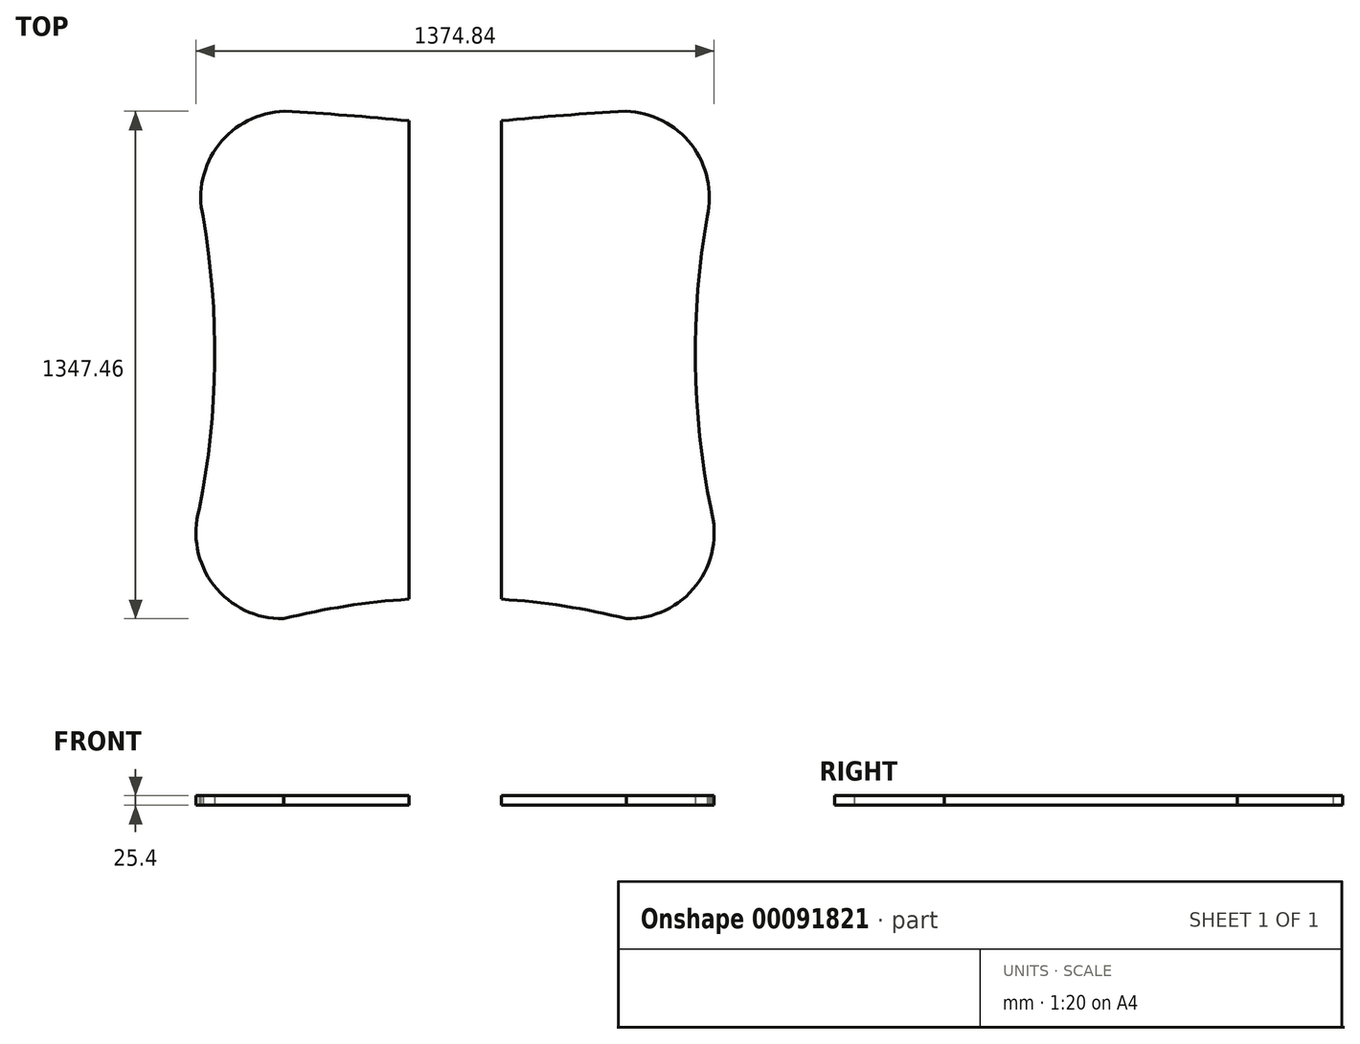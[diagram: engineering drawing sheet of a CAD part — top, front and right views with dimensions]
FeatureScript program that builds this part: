
annotation { "Feature Type Name" : "Feature", "Feature Type Description" : "" }
export const myFeature = defineFeature(function(context is Context, id is Id, definition is map)
    precondition{}
    {
        {
            var Q0;
            Q0=qCreatedBy(makeId("Top.planeOp"),FACE);
            var sketch = newSketch(context, id + "F0", { "sketchPlane" : qUnion([Q0])});
            skLineSegment(sketch, "E0", {"start": v(-122.75, 617.41) * mm, "end": v(-122.75, 363.41) * mm});
            skArc(sketch, "E1", {"start": v(-678.8, -413.88) * mm, "mid": v(-637.61, -25.7) * mm, "end": v(-668.85, 363.41) * mm});
            skArc(sketch, "E2", {"start": v(-452.95, 642.81) * mm, "mid": v(-626.87, 554.1) * mm, "end": v(-668.85, 363.41) * mm});
            skArc(sketch, "E3", {"start": v(-678.8, -413.88) * mm, "mid": v(-639.9, -615.57) * mm, "end": v(-454.8, -704.61) * mm});
            skLineSegment(sketch, "E4", {"start": v(-122.75, 617.41) * mm, "end": v(-122.75, -652.59) * mm});
            skArc(sketch, "E5", {"start": v(-122.75, 617.41) * mm, "mid": v(-287.7, 632.1) * mm, "end": v(-452.95, 642.81) * mm});
            skArc(sketch, "E6", {"start": v(-122.75, -652.59) * mm, "mid": v(-289.94, -671.12) * mm, "end": v(-454.8, -704.61) * mm});
            skSolve(sketch);
        }
        {
            var Q0;
            Q0=makeQuery(id+"F0.imprint","IMPRINT",FACE,{"disambiguationData":[TD([[makeQuery(id+"F0.imprint","IMPRINT",EDGE,{"derivedFrom":sQuery(id+"F0.wireOp",EDGE,"e7358e8d-3bd0-44fc-b618-9dafbb7d24566.MirrorCS")}),1.0]])]});
            var Q1;
            {var subQ0=sQuery(id+"F0.wireOp",EDGE,"E4");var subQ3=makeQuery(id+"F0.imprint","IMPRINT",VERTEX,{"derivedFrom":subQ0});Q1=makeQuery(id+"F0.imprint","IMPRINT",FACE,{"disambiguationData":[TD([[makeQuery(id+"F0.imprint","IMPRINT",EDGE,{"disambiguationData":[TD([[subQ3,1.0]])],"derivedFrom":subQ0}),1.0]])]});}
            var Q2;
            Q2=makeQuery(id+"F0.imprint","IMPRINT",FACE,{"disambiguationData":[TD([[makeQuery(id+"F0.imprint","IMPRINT",EDGE,{"derivedFrom":sQuery(id+"F0.wireOp",EDGE,"E1")}),-1.0]])]});
            extrude(context, id + "F1", {"entities" : qUnion([Q0, Q1, Q2]), "depth" : 25.4 * mm});
        }
        {
            var Q0;
            Q0=makeQuery(id+"F1.opExtrude","SWEPT_BODY",BODY,{"disambiguationData":[OSD([sQuery(id+"F0.wireOp",EDGE,"E1"),sQuery(id+"F0.wireOp",EDGE,"E2"),sQuery(id+"F0.wireOp",EDGE,"E3"),sQuery(id+"F0.wireOp",EDGE,"E4"),sQuery(id+"F0.wireOp",EDGE,"E5"),sQuery(id+"F0.wireOp",EDGE,"E6")])]});
            var Q1;
            Q1=qCreatedBy(makeId("Right.planeOp"),FACE);
            mirror(context, id + "F2", {"entities" : qUnion([Q0]), "mirrorPlane" : qUnion([Q1])});
        }
    });
